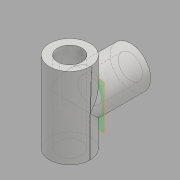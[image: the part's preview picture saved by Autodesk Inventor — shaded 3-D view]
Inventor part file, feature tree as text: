
AUTODESK INVENTOR PART (.ipt)
format: ipt  version: 2017 (Build 210142000, 142)  size: 109,568 bytes
history: native  units: mm
features: extrude x6, sketch x6, plane x1
ambient origin geometry x8: Origin, YZ Plane, XZ Plane, XY Plane, X Axis, Y Axis, Z Axis, Center Point
bodies: Solid1 (feature_tree)
feature tree (13):
  extrude  "Extrusion1"  Depth=20.0mm TaperAngle=0.0deg
  extrude  "Extrusion3"  Depth=15.0mm
  extrude  "Extrusion2"  Depth=20.0mm TaperAngle=0.0deg
  extrude  "Extrusion4"  Depth=2.0mm TaperAngle=0.0deg
  extrude  "Extrusion5"  [1 undecoded]
  plane  "Work Plane2"
  extrude  "Extrusion6"  [1 undecoded]
  sketch  "Sketch1"  dims[d0=10.0mm d1=10.0mm d2=0.0mm d3=0.0mm d4=20.0mm d5=0.0mm]
  sketch  "Sketch2"  dims[d6=15.0mm d7=0.0mm d8=6.0mm]
  sketch  "Sketch3"  dims[d9=10.0mm d10=0.0mm d12=20.0mm d13=0.0mm]
  sketch  "Sketch4"  dims[d14=-12.0mm d15=2.0mm d16=0.0mm]
  sketch  "Sketch5"
  sketch  "Sketch6"
note: 2 required parameter values undecoded (feature->parameter linkage not recoverable at this tier; creation-order binding heuristic only, values carry confidence <= 0.55)
